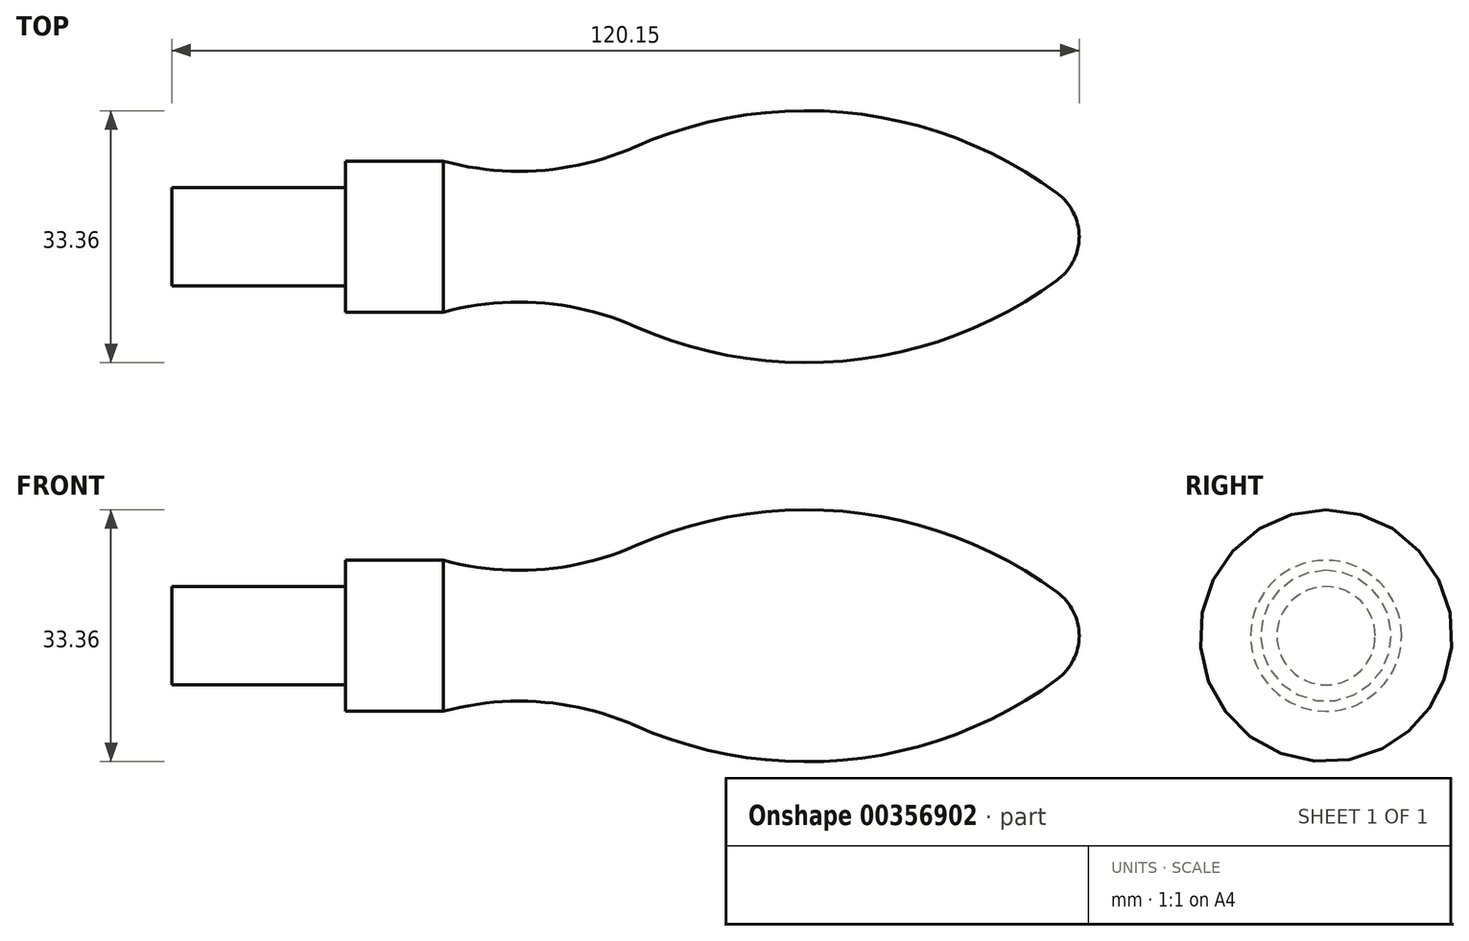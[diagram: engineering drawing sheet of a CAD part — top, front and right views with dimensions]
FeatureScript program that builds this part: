
annotation { "Feature Type Name" : "Feature", "Feature Type Description" : "" }
export const myFeature = defineFeature(function(context is Context, id is Id, definition is map)
    precondition{}
    {
        {
            var Q0;
            Q0=qCreatedBy(makeId("Top.planeOp"),FACE);
            var sketch = newSketch(context, id + "F0", { "sketchPlane" : qUnion([Q0])});
            skLineSegment(sketch, "E0", {"start": v(0, -76.14) * mm, "end": v(0, 79.23) * mm, "construction": true});
            skLineSegment(sketch, "E1", {"start": v(-134.87, 0) * mm, "end": v(126.42, 0) * mm, "construction": true});
            skLineSegment(sketch, "E2", {"start": v(-38, 78.8) * mm, "end": v(-38, -79.7) * mm, "construction": true});
            skLineSegment(sketch, "E3", {"start": v(-61, 76.57) * mm, "end": v(-61, -78.2) * mm, "construction": true});
            skPoint(sketch, "E4", {"position": v(-61, 0) * mm});
            skPoint(sketch, "E5", {"position": v(-61, 6.5) * mm});
            skPoint(sketch, "E6", {"position": v(-61, -6.5) * mm});
            skLineSegment(sketch, "E7.bottom", {"start": v(-61, -6.5) * mm, "end": v(-84, -6.5) * mm});
            skLineSegment(sketch, "E7.left", {"start": v(-61, -6.5) * mm, "end": v(-61, 6.5) * mm});
            skLineSegment(sketch, "E7.right", {"start": v(-84, -6.5) * mm, "end": v(-84, 0) * mm});
            skPoint(sketch, "E8", {"position": v(-61, 10) * mm});
            skPoint(sketch, "E9", {"position": v(-61, -10) * mm});
            skLineSegment(sketch, "E10.bottom", {"start": v(-61, -10) * mm, "end": v(-61, -10) * mm});
            skLineSegment(sketch, "E10.top", {"start": v(-61, 10) * mm, "end": v(-61, 10) * mm});
            skLineSegment(sketch, "E10.left", {"start": v(-61, -10) * mm, "end": v(-61, 10) * mm});
            skLineSegment(sketch, "E10.right", {"start": v(-61, -10) * mm, "end": v(-61, 10) * mm});
            skLineSegment(sketch, "E11.bottom", {"start": v(-61, -10) * mm, "end": v(-48, -10) * mm});
            skArc(sketch, "E12", {"start": v(-84.66, 0) * mm, "mid": v(-11.65, -21.09) * mm, "end": v(-84, 2.17) * mm, "construction": true});
            skPoint(sketch, "E13", {"position": v(-38, -46.66) * mm});
            skCircle(sketch, "E14", {"center": v(-38, -46.66) * mm, "radius": 94 * mm, "construction": true});
            skPoint(sketch, "E15", {"position": v(0, 39.32) * mm});
            skPoint(sketch, "E16", {"position": v(29, 0) * mm});
            skArc(sketch, "E17", {"start": v(33.24, -5.75) * mm, "mid": v(35.38, -3.22) * mm, "end": v(36.15, 0) * mm});
            skArc(sketch, "E18.trimOffspring", {"start": v(-22.64, -11.9) * mm, "mid": v(-35.16, -8.77) * mm, "end": v(-48, -10) * mm});
            skArc(sketch, "E19.trimOffspring", {"start": v(-22.64, -11.9) * mm, "mid": v(6.13, -16.35) * mm, "end": v(33.24, -5.75) * mm});
            skLineSegment(sketch, "E20", {"start": v(-61, 0) * mm, "end": v(36.15, 0) * mm});
            skPoint(sketch, "E11.top.end.orphan", {"position": v(-48, 10) * mm});
            skPoint(sketch, "E7.top.end.orphan", {"position": v(-84, 6.5) * mm});
            skLineSegment(sketch, "E21", {"start": v(-84, 0) * mm, "end": v(-61, 0) * mm});
            skLineSegment(sketch, "E22", {"start": v(-84, 0) * mm, "end": v(36.15, 0) * mm});
            skSolve(sketch);
        }
        {
            var Q0;
            {var subQ5=sQuery(id+"F0.wireOp",EDGE,"E11.bottom");Q0=makeQuery(id+"F0.imprint","IMPRINT",FACE,{"disambiguationData":[TD([[makeQuery(id+"F0.imprint","IMPRINT",EDGE,{"derivedFrom":subQ5}),1.0]])]});}
            var Q1;
            Q1=sQuery(id+"F0.wireOp",EDGE,"E1");
            revolve(context, id + "F1", {"entities" : qUnion([Q0]), "axis" : qUnion([Q1]), "revolveType" : RevolveType.FULL});
        }
        {
            var Q0;
            {var subQ0=sQuery(id+"F0.wireOp",EDGE,"E7.bottom");Q0=makeQuery(id+"F0.imprint","IMPRINT",FACE,{"disambiguationData":[TD([[makeQuery(id+"F0.imprint","IMPRINT",EDGE,{"derivedFrom":subQ0}),-1.0]])]});}
            var Q1;
            Q1=sQuery(id+"F0.wireOp",EDGE,"E1");
            revolve(context, id + "F2", {"operationType" : NewBodyOperationType.ADD, "entities" : qUnion([Q0]), "axis" : qUnion([Q1]), "revolveType" : RevolveType.FULL});
        }
    });
